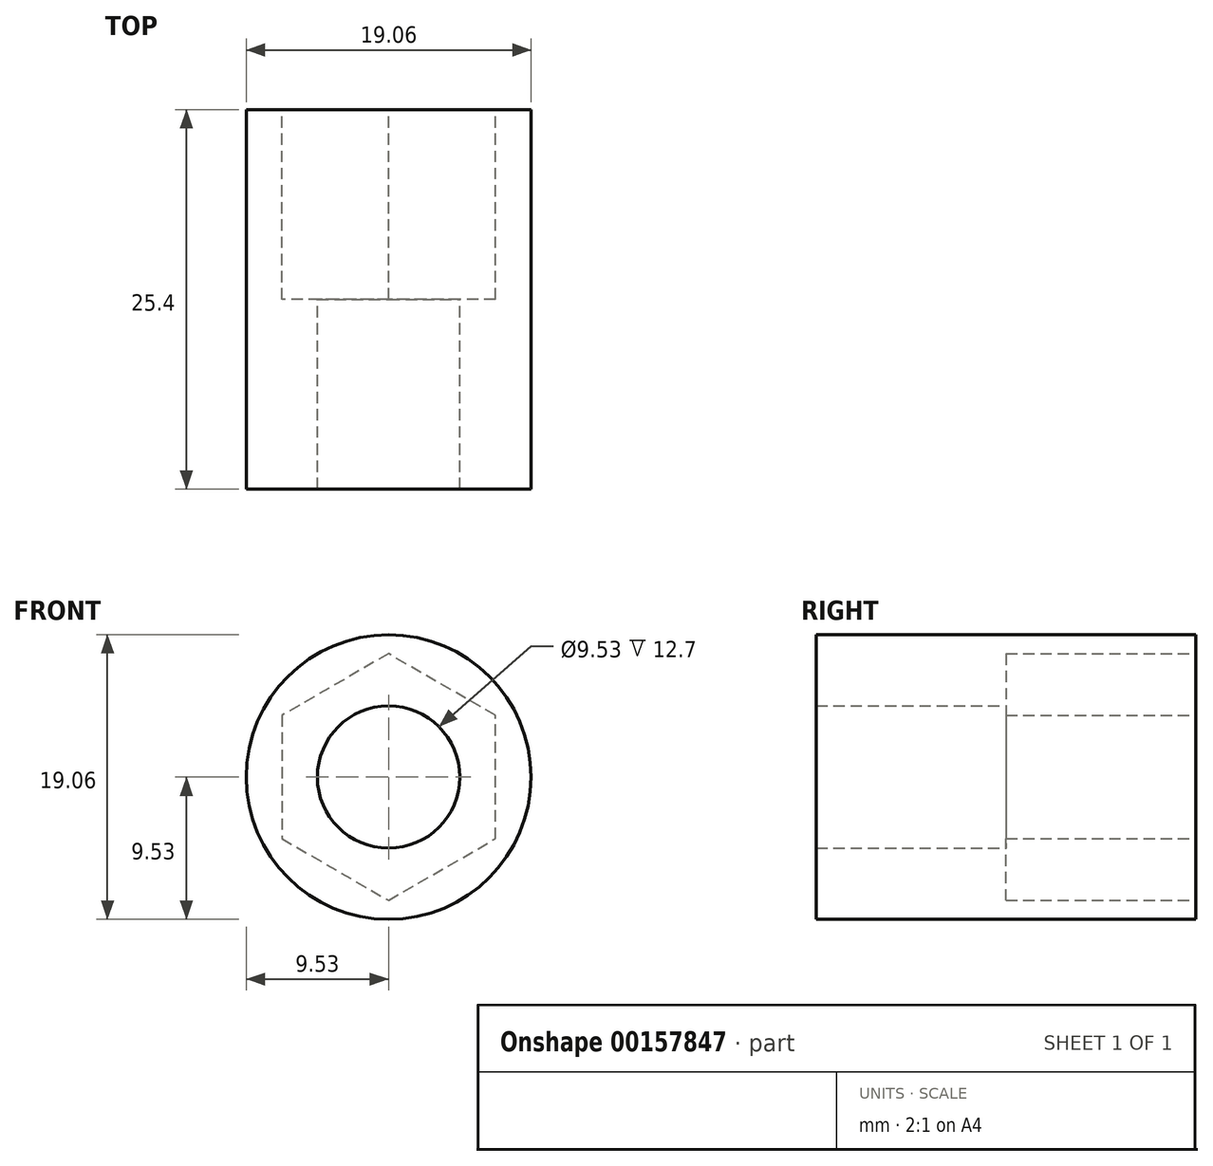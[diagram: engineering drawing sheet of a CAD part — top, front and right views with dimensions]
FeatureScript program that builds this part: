
annotation { "Feature Type Name" : "Feature", "Feature Type Description" : "" }
export const myFeature = defineFeature(function(context is Context, id is Id, definition is map)
    precondition{}
    {
        {
            var Q0;
            Q0=qCreatedBy(makeId("Front.planeOp"),FACE);
            var sketch = newSketch(context, id + "F0", { "sketchPlane" : qUnion([Q0])});
            skCircle(sketch, "E0", {"center": v(0, 0) * mm, "radius": 9.53 * mm});
            skSolve(sketch);
        }
        {
            var Q0;
            Q0 = qSketchRegion(id + "F0", true);
            extrude(context, id + "F1", {"entities" : qUnion([Q0]), "depth" : 25.4 * mm});
        }
        {
            var Q0;
            Q0=qCreatedBy(makeId("Front.planeOp"),FACE);
            var sketch = newSketch(context, id + "F2", { "sketchPlane" : qUnion([Q0])});
            skLineSegment(sketch, "E1.bottom", {"start": v(4.76, -4.76) * mm, "end": v(-4.76, -4.76) * mm});
            skLineSegment(sketch, "E1.top", {"start": v(4.76, 4.76) * mm, "end": v(-4.76, 4.76) * mm});
            skLineSegment(sketch, "E1.left", {"start": v(4.76, -4.76) * mm, "end": v(4.76, 4.76) * mm});
            skLineSegment(sketch, "E1.right", {"start": v(-4.76, -4.76) * mm, "end": v(-4.76, 4.76) * mm});
            skPoint(sketch, "E1.middle", {"position": v(0, 0) * mm});
            skCircle(sketch, "E2", {"center": v(0, 0) * mm, "radius": 4.76 * mm});
            skSolve(sketch);
        }
        {
            var Q0;
            Q0 = qSketchRegion(id + "F2", true);
            extrude(context, id + "F3", {"entities" : qUnion([Q0]), "operationType" : NewBodyOperationType.ADD, "depth" : 25.4 * mm});
        }
        {
            var Q0;
            Q0=qCreatedBy(makeId("Front.planeOp"),FACE);
            var sketch = newSketch(context, id + "F4", { "sketchPlane" : qUnion([Q0])});
            skLineSegment(sketch, "E3.bottom", {"start": v(4.76, -4.76) * mm, "end": v(-4.76, -4.76) * mm});
            skLineSegment(sketch, "E3.top", {"start": v(4.76, 4.76) * mm, "end": v(-4.76, 4.76) * mm});
            skLineSegment(sketch, "E3.left", {"start": v(4.76, -4.76) * mm, "end": v(4.76, 4.76) * mm});
            skLineSegment(sketch, "E3.right", {"start": v(-4.76, -4.76) * mm, "end": v(-4.76, 4.76) * mm});
            skPoint(sketch, "E3.middle", {"position": v(0, 0) * mm});
            skCircle(sketch, "E4", {"center": v(0, 0) * mm, "radius": 4.76 * mm});
            skSolve(sketch);
        }
        {
            var Q0;
            {var subQ0=sQuery(id+"F4.wireOp",EDGE,"E4");var subQ1=makeQuery(id+"F4.imprint","INTERSECT",VERTEX,{"derivedFrom":[sQuery(id+"F4.wireOp",EDGE,"E3.top"),subQ0]});Q0=makeQuery(id+"F4.imprint","IMPRINT",FACE,{"disambiguationData":[TD([[makeQuery(id+"F4.imprint","IMPRINT",EDGE,{"disambiguationData":[TD([[subQ1,1.0]])],"derivedFrom":subQ0}),1.0]])]});}
            extrude(context, id + "F5", {"entities" : qUnion([Q0]), "operationType" : NewBodyOperationType.REMOVE, "endBound" : BoundingType.THROUGH_ALL, "depth" : 25.4 * mm});
        }
        {
            var Q0;
            Q0 = qSketchRegion(id + "F4", true);
            extrude(context, id + "F6", {"entities" : qUnion([Q0]), "operationType" : NewBodyOperationType.REMOVE, "depth" : 9.52 * mm});
        }
        {
            var Q0;
            Q0=makeQuery(id+"F1.opExtrude","CAP_FACE",FACE,{"disambiguationData":[OSD([sQuery(id+"F0.wireOp",EDGE,"E0")])],"isStart":true});
            var sketch = newSketch(context, id + "F7", { "sketchPlane" : qUnion([Q0])});
            skCircle(sketch, "E5.cCircle", {"center": v(0, 0) * mm, "radius": 7.15 * mm, "construction": true});
            skLineSegment(sketch, "E5.0", {"start": v(7.15, 4.13) * mm, "end": v(7.15, -4.13) * mm});
            skLineSegment(sketch, "E5.1", {"start": v(7.15, -4.13) * mm, "end": v(0, -8.25) * mm});
            skLineSegment(sketch, "E5.2", {"start": v(0, -8.25) * mm, "end": v(-7.15, -4.13) * mm});
            skLineSegment(sketch, "E5.3", {"start": v(-7.15, -4.13) * mm, "end": v(-7.15, 4.13) * mm});
            skLineSegment(sketch, "E5.4", {"start": v(-7.15, 4.13) * mm, "end": v(0, 8.25) * mm});
            skLineSegment(sketch, "E5.5", {"start": v(0, 8.25) * mm, "end": v(7.15, 4.13) * mm});
            skPoint(sketch, "E5.0.midPoint", {"position": v(7.15, 0) * mm});
            skSolve(sketch);
        }
        {
            var Q0;
            Q0 = qSketchRegion(id + "F7", true);
            extrude(context, id + "F8", {"entities" : qUnion([Q0]), "operationType" : NewBodyOperationType.REMOVE, "oppositeDirection" : true, "depth" : 12.7 * mm});
        }
    });
